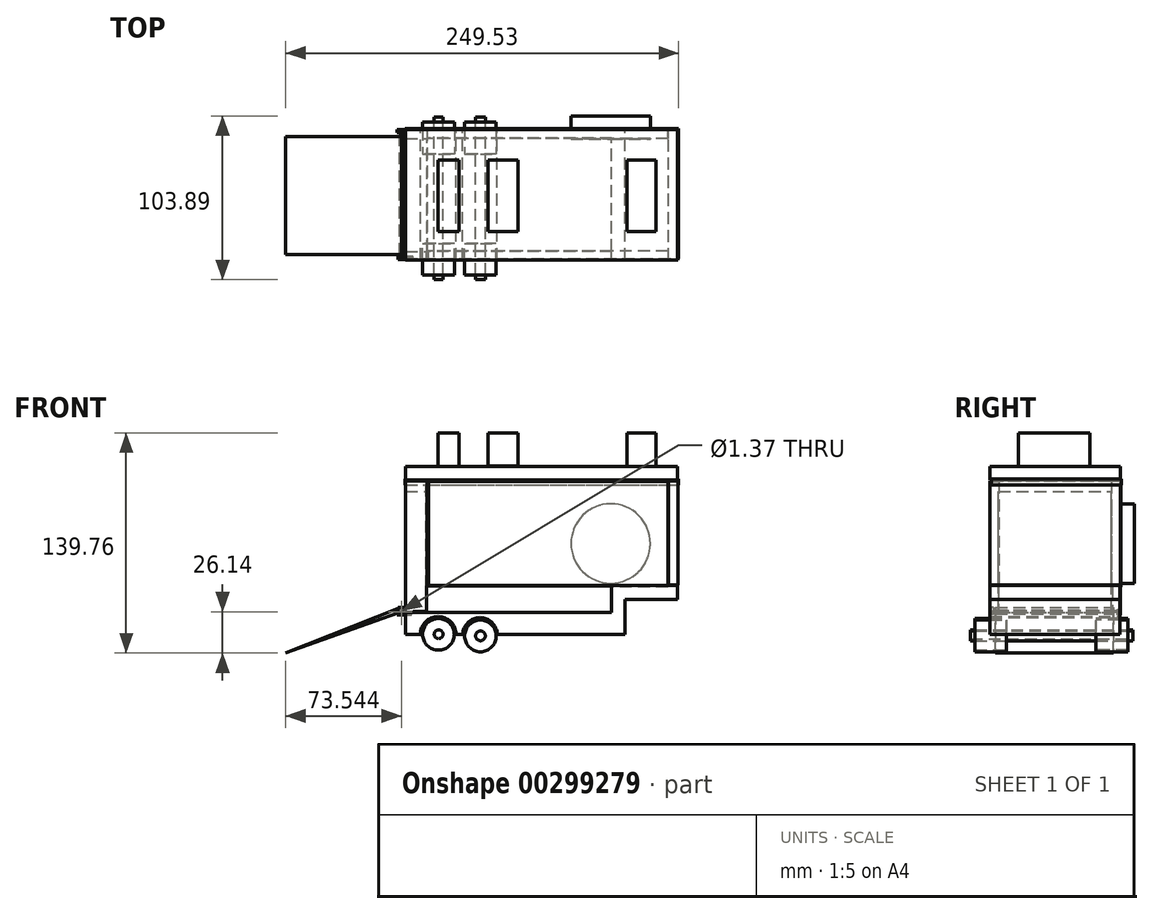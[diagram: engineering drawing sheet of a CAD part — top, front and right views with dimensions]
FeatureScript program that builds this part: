
annotation { "Feature Type Name" : "Feature", "Feature Type Description" : "" }
export const myFeature = defineFeature(function(context is Context, id is Id, definition is map)
    precondition{}
    {
        {
            var Q0;
            Q0=qCreatedBy(makeId("Front.planeOp"),FACE);
            var sketch = newSketch(context, id + "F0", { "sketchPlane" : qUnion([Q0])});
            skLineSegment(sketch, "E0", {"start": v(71.12, -5.98) * mm, "end": v(29.44, -5.98) * mm});
            skLineSegment(sketch, "E1", {"start": v(29.44, -5.98) * mm, "end": v(29.44, -23.17) * mm});
            skLineSegment(sketch, "E2", {"start": v(29.44, -23.17) * mm, "end": v(-101.43, -23.17) * mm});
            skLineSegment(sketch, "E3", {"start": v(-101.43, -23.17) * mm, "end": v(-101.43, -37.16) * mm});
            skLineSegment(sketch, "E4", {"start": v(-101.43, -37.16) * mm, "end": v(37.9, -37.16) * mm});
            skLineSegment(sketch, "E5", {"start": v(37.9, -37.16) * mm, "end": v(37.9, -15.01) * mm});
            skLineSegment(sketch, "E6", {"start": v(37.9, -15.01) * mm, "end": v(71.12, -15.01) * mm});
            skLineSegment(sketch, "E7", {"start": v(71.12, -15.01) * mm, "end": v(71.12, -5.98) * mm});
            skSolve(sketch);
        }
        {
            var Q0;
            Q0 = qSketchRegion(id + "F0", true);
            extrude(context, id + "F1", {"entities" : qUnion([Q0]), "depth" : 38.86 * mm, "hasSecondDirection" : true, "secondDirectionOppositeDirection" : true, "secondDirectionDepth" : 43.43 * mm});
        }
        {
            var Q0;
            Q0=qCreatedBy(makeId("Front.planeOp"),FACE);
            var sketch = newSketch(context, id + "F2", { "sketchPlane" : qUnion([Q0])});
            skCircle(sketch, "E8", {"center": v(-80.74, -37.16) * mm, "radius": 11.34 * mm});
            skCircle(sketch, "E9", {"center": v(-54.21, -37.45) * mm, "radius": 10.96 * mm});
            skSolve(sketch);
        }
        {
            var Q0;
            Q0 = qSketchRegion(id + "F2", true);
            extrude(context, id + "F3", {"entities" : qUnion([Q0]), "operationType" : NewBodyOperationType.REMOVE, "depth" : 43.94 * mm, "hasSecondDirection" : true, "secondDirectionOppositeDirection" : true, "secondDirectionDepth" : 49.28 * mm});
        }
        {
            var Q0;
            Q0=qCreatedBy(makeId("Front.planeOp"),FACE);
            var sketch = newSketch(context, id + "F4", { "sketchPlane" : qUnion([Q0])});
            skLineSegment(sketch, "E10.bottom", {"start": v(29.86, -6.27) * mm, "end": v(-15.61, -6.27) * mm});
            skLineSegment(sketch, "E10.top", {"start": v(29.86, -23.17) * mm, "end": v(-15.61, -23.17) * mm});
            skLineSegment(sketch, "E10.left", {"start": v(29.86, -6.27) * mm, "end": v(29.86, -23.17) * mm});
            skLineSegment(sketch, "E10.right", {"start": v(-15.61, -6.27) * mm, "end": v(-15.61, -23.17) * mm});
            skLineSegment(sketch, "E11.bottom", {"start": v(-15.61, -6.27) * mm, "end": v(-88.2, -6.27) * mm});
            skLineSegment(sketch, "E11.top", {"start": v(-15.61, -23.17) * mm, "end": v(-88.2, -23.17) * mm});
            skLineSegment(sketch, "E11.right", {"start": v(-88.2, -6.27) * mm, "end": v(-88.2, -23.17) * mm});
            skSolve(sketch);
        }
        {
            var Q0;
            Q0 = qSketchRegion(id + "F4", true);
            extrude(context, id + "F5", {"entities" : qUnion([Q0]), "operationType" : NewBodyOperationType.ADD, "depth" : 38.6 * mm, "hasSecondDirection" : true, "secondDirectionOppositeDirection" : false, "secondDirectionDepth" : 33.53 * mm});
        }
        {
            var Q0;
            Q0=qCreatedBy(makeId("Front.planeOp"),FACE);
            var sketch = newSketch(context, id + "F6", { "sketchPlane" : qUnion([Q0])});
            skLineSegment(sketch, "E12.bottom", {"start": v(29.44, -6.56) * mm, "end": v(-22.15, -6.56) * mm});
            skLineSegment(sketch, "E12.top", {"start": v(29.44, -23.17) * mm, "end": v(-22.15, -23.17) * mm});
            skLineSegment(sketch, "E12.left", {"start": v(29.44, -6.56) * mm, "end": v(29.44, -23.17) * mm});
            skLineSegment(sketch, "E12.right", {"start": v(-22.15, -6.56) * mm, "end": v(-22.15, -23.17) * mm});
            skLineSegment(sketch, "E13.bottom", {"start": v(-22.15, -6.56) * mm, "end": v(-88.03, -6.56) * mm});
            skLineSegment(sketch, "E13.top", {"start": v(-22.15, -23.17) * mm, "end": v(-88.03, -23.17) * mm});
            skLineSegment(sketch, "E13.right", {"start": v(-88.03, -6.56) * mm, "end": v(-88.03, -23.17) * mm});
            skSolve(sketch);
        }
        {
            var Q0;
            Q0 = qSketchRegion(id + "F6", true);
            extrude(context, id + "F7", {"entities" : qUnion([Q0]), "operationType" : NewBodyOperationType.ADD, "oppositeDirection" : true, "depth" : 43.43 * mm, "hasSecondDirection" : true, "secondDirectionOppositeDirection" : true, "secondDirectionDepth" : 38.6 * mm});
        }
        {
            var Q0;
            Q0=qCreatedBy(makeId("Right.planeOp"),FACE);
            var sketch = newSketch(context, id + "F8", { "sketchPlane" : qUnion([Q0])});
            skLineSegment(sketch, "E14.bottom", {"start": v(43.93, -23.17) * mm, "end": v(38.1, -23.17) * mm});
            skLineSegment(sketch, "E14.top", {"start": v(43.93, 60.48) * mm, "end": v(38.1, 60.48) * mm});
            skLineSegment(sketch, "E14.left", {"start": v(43.93, -23.17) * mm, "end": v(43.93, 60.48) * mm});
            skLineSegment(sketch, "E14.right", {"start": v(38.1, -23.17) * mm, "end": v(38.1, 60.48) * mm});
            skLineSegment(sketch, "E15.bottom", {"start": v(-33.6, -22.59) * mm, "end": v(-38.56, -22.59) * mm});
            skLineSegment(sketch, "E15.top", {"start": v(-33.6, 60.48) * mm, "end": v(-38.56, 60.48) * mm});
            skLineSegment(sketch, "E15.left", {"start": v(-33.6, -22.59) * mm, "end": v(-33.6, 60.48) * mm});
            skLineSegment(sketch, "E15.right", {"start": v(-38.56, -22.59) * mm, "end": v(-38.56, 60.48) * mm});
            skLineSegment(sketch, "E16.bottom", {"start": v(-33.6, 60.48) * mm, "end": v(38.1, 60.48) * mm});
            skLineSegment(sketch, "E16.top", {"start": v(-33.6, 53.78) * mm, "end": v(38.1, 53.78) * mm});
            skLineSegment(sketch, "E16.left", {"start": v(-33.6, 60.48) * mm, "end": v(-33.6, 53.78) * mm});
            skLineSegment(sketch, "E16.right", {"start": v(38.1, 60.48) * mm, "end": v(38.1, 53.78) * mm});
            skSolve(sketch);
        }
        {
            var Q0;
            Q0 = qSketchRegion(id + "F8", true);
            extrude(context, id + "F9", {"entities" : qUnion([Q0]), "operationType" : NewBodyOperationType.ADD, "oppositeDirection" : true, "depth" : 101.35 * mm, "hasSecondDirection" : true, "secondDirectionOppositeDirection" : true, "secondDirectionDepth" : 87.88 * mm});
        }
        {
            var Q0;
            Q0=qCreatedBy(makeId("Front.planeOp"),FACE);
            var sketch = newSketch(context, id + "F10", { "sketchPlane" : qUnion([Q0])});
            skLineSegment(sketch, "E17", {"start": v(-104.1, -22.8) * mm, "end": v(-177.64, -48.94) * mm});
            skLineSegment(sketch, "E18", {"start": v(-177.64, -48.94) * mm, "end": v(-104.1, -19.93) * mm});
            skLineSegment(sketch, "E19", {"start": v(-104.1, -19.93) * mm, "end": v(-104.1, -22.8) * mm});
            skCircle(sketch, "E20", {"center": v(-104.1, -22.8) * mm, "radius": 0.69 * mm});
            skCircle(sketch, "E21", {"center": v(-104.1, -22.8) * mm, "radius": 1.32 * mm});
            skSolve(sketch);
        }
        {
            var Q0;
            Q0 = qSketchRegion(id + "F10", true);
            extrude(context, id + "F11", {"entities" : qUnion([Q0]), "operationType" : NewBodyOperationType.ADD, "depth" : 35.56 * mm, "hasSecondDirection" : true, "secondDirectionOppositeDirection" : true, "secondDirectionDepth" : 39.37 * mm});
        }
        {
            var Q0;
            Q0=qCreatedBy(makeId("Front.planeOp"),FACE);
            var sketch = newSketch(context, id + "F12", { "sketchPlane" : qUnion([Q0])});
            skLineSegment(sketch, "E22.bottom", {"start": v(71.52, -5.74) * mm, "end": v(65.43, -5.74) * mm});
            skLineSegment(sketch, "E22.top", {"start": v(71.52, 60.34) * mm, "end": v(65.43, 60.34) * mm});
            skLineSegment(sketch, "E22.left", {"start": v(71.52, -5.74) * mm, "end": v(71.52, 60.34) * mm});
            skLineSegment(sketch, "E22.right", {"start": v(65.43, -5.74) * mm, "end": v(65.43, 60.34) * mm});
            skSolve(sketch);
        }
        {
            var Q0;
            Q0 = qSketchRegion(id + "F12", true);
            extrude(context, id + "F13", {"entities" : qUnion([Q0]), "depth" : 39.12 * mm, "hasSecondDirection" : true, "secondDirectionOppositeDirection" : true, "secondDirectionDepth" : 43.94 * mm});
        }
        {
            var Q0;
            Q0=qCreatedBy(makeId("Front.planeOp"),FACE);
            var sketch = newSketch(context, id + "F14", { "sketchPlane" : qUnion([Q0])});
            skLineSegment(sketch, "E23.bottom", {"start": v(65.1, 60.02) * mm, "end": v(0, 60.02) * mm});
            skLineSegment(sketch, "E23.top", {"start": v(65.1, -6.06) * mm, "end": v(0, -6.06) * mm});
            skLineSegment(sketch, "E23.left", {"start": v(65.1, 60.02) * mm, "end": v(65.1, -6.06) * mm});
            skLineSegment(sketch, "E23.right", {"start": v(0, 60.02) * mm, "end": v(0, -6.06) * mm});
            skLineSegment(sketch, "E24.bottom", {"start": v(0, 60.02) * mm, "end": v(-86.94, 60.02) * mm});
            skLineSegment(sketch, "E24.top", {"start": v(0, -6.06) * mm, "end": v(-86.94, -6.06) * mm});
            skLineSegment(sketch, "E24.right", {"start": v(-86.94, 60.02) * mm, "end": v(-86.94, -6.06) * mm});
            skSolve(sketch);
        }
        {
            var Q0;
            Q0 = qSketchRegion(id + "F14", true);
            extrude(context, id + "F15", {"entities" : qUnion([Q0]), "operationType" : NewBodyOperationType.ADD, "depth" : 39.12 * mm, "hasSecondDirection" : true, "secondDirectionOppositeDirection" : false, "secondDirectionDepth" : 33.27 * mm});
        }
        {
            var Q0;
            Q0=qCreatedBy(makeId("Front.planeOp"),FACE);
            var sketch = newSketch(context, id + "F16", { "sketchPlane" : qUnion([Q0])});
            skLineSegment(sketch, "E25.bottom", {"start": v(65.1, 60.02) * mm, "end": v(0, 60.02) * mm});
            skLineSegment(sketch, "E25.top", {"start": v(65.1, -7.02) * mm, "end": v(0, -7.02) * mm});
            skLineSegment(sketch, "E25.left", {"start": v(65.1, 60.02) * mm, "end": v(65.1, -7.02) * mm});
            skLineSegment(sketch, "E25.right", {"start": v(0, 60.02) * mm, "end": v(0, -7.02) * mm});
            skLineSegment(sketch, "E26.bottom", {"start": v(0, 60.02) * mm, "end": v(-88.54, 60.02) * mm});
            skLineSegment(sketch, "E26.top", {"start": v(0, -7.02) * mm, "end": v(-88.54, -7.02) * mm});
            skLineSegment(sketch, "E26.right", {"start": v(-88.54, 60.02) * mm, "end": v(-88.54, -7.02) * mm});
            skSolve(sketch);
        }
        {
            var Q0;
            Q0 = qSketchRegion(id + "F16", true);
            extrude(context, id + "F17", {"entities" : qUnion([Q0]), "operationType" : NewBodyOperationType.ADD, "oppositeDirection" : true, "depth" : 44.2 * mm, "hasSecondDirection" : true, "secondDirectionOppositeDirection" : true, "secondDirectionDepth" : 38.1 * mm});
        }
        {
            var Q0;
            Q0=qCreatedBy(makeId("Front.planeOp"),FACE);
            var sketch = newSketch(context, id + "F18", { "sketchPlane" : qUnion([Q0])});
            skLineSegment(sketch, "E27.bottom", {"start": v(71.11, 60.98) * mm, "end": v(-29.61, 60.98) * mm});
            skLineSegment(sketch, "E27.top", {"start": v(71.11, 69.64) * mm, "end": v(-29.61, 69.64) * mm});
            skLineSegment(sketch, "E27.left", {"start": v(71.11, 60.98) * mm, "end": v(71.11, 69.64) * mm});
            skLineSegment(sketch, "E27.right", {"start": v(-29.61, 60.98) * mm, "end": v(-29.61, 69.64) * mm});
            skLineSegment(sketch, "E28.bottom", {"start": v(-29.61, 60.98) * mm, "end": v(-101.46, 60.98) * mm});
            skLineSegment(sketch, "E28.top", {"start": v(-29.61, 69.64) * mm, "end": v(-101.46, 69.64) * mm});
            skLineSegment(sketch, "E28.right", {"start": v(-101.46, 60.98) * mm, "end": v(-101.46, 69.64) * mm});
            skSolve(sketch);
        }
        {
            var Q0;
            Q0 = qSketchRegion(id + "F18", true);
            extrude(context, id + "F19", {"entities" : qUnion([Q0]), "depth" : 38.86 * mm, "hasSecondDirection" : true, "secondDirectionOppositeDirection" : true, "secondDirectionDepth" : 43.94 * mm});
        }
        {
            var Q0;
            Q0=qCreatedBy(makeId("Front.planeOp"),FACE);
            var sketch = newSketch(context, id + "F20", { "sketchPlane" : qUnion([Q0])});
            skLineSegment(sketch, "E29.bottom", {"start": v(-67.37, 68.68) * mm, "end": v(-80.85, 68.68) * mm});
            skLineSegment(sketch, "E29.top", {"start": v(-67.37, 90.82) * mm, "end": v(-80.85, 90.82) * mm});
            skLineSegment(sketch, "E29.left", {"start": v(-67.37, 68.68) * mm, "end": v(-67.37, 90.82) * mm});
            skLineSegment(sketch, "E29.right", {"start": v(-80.85, 68.68) * mm, "end": v(-80.85, 90.82) * mm});
            skLineSegment(sketch, "E30.bottom", {"start": v(-30.16, 69.97) * mm, "end": v(-49.09, 69.97) * mm});
            skLineSegment(sketch, "E30.top", {"start": v(-30.16, 90.82) * mm, "end": v(-49.09, 90.82) * mm});
            skLineSegment(sketch, "E30.left", {"start": v(-30.16, 69.97) * mm, "end": v(-30.16, 90.82) * mm});
            skLineSegment(sketch, "E30.right", {"start": v(-49.09, 69.97) * mm, "end": v(-49.09, 90.82) * mm});
            skLineSegment(sketch, "E31.bottom", {"start": v(57.73, 69.64) * mm, "end": v(39.12, 69.64) * mm});
            skLineSegment(sketch, "E31.top", {"start": v(57.73, 90.82) * mm, "end": v(39.12, 90.82) * mm});
            skLineSegment(sketch, "E31.left", {"start": v(57.73, 69.64) * mm, "end": v(57.73, 90.82) * mm});
            skLineSegment(sketch, "E31.right", {"start": v(39.12, 69.64) * mm, "end": v(39.12, 90.82) * mm});
            skSolve(sketch);
        }
        {
            var Q0;
            Q0 = qSketchRegion(id + "F20", true);
            extrude(context, id + "F21", {"entities" : qUnion([Q0]), "operationType" : NewBodyOperationType.ADD, "depth" : 20.83 * mm, "hasSecondDirection" : true, "secondDirectionOppositeDirection" : true, "secondDirectionDepth" : 24.38 * mm});
        }
        {
            var Q0;
            Q0=qCreatedBy(makeId("Front.planeOp"),FACE);
            var sketch = newSketch(context, id + "F22", { "sketchPlane" : qUnion([Q0])});
            skLineSegment(sketch, "E32.bottom", {"start": v(-101.88, 61.45) * mm, "end": v(71.9, 61.45) * mm});
            skLineSegment(sketch, "E32.top", {"start": v(-101.88, 57.94) * mm, "end": v(71.9, 57.94) * mm});
            skLineSegment(sketch, "E32.left", {"start": v(-101.88, 61.45) * mm, "end": v(-101.88, 57.94) * mm});
            skLineSegment(sketch, "E32.right", {"start": v(71.9, 61.45) * mm, "end": v(71.9, 57.94) * mm});
            skSolve(sketch);
        }
        {
            var Q0;
            Q0 = qSketchRegion(id + "F22", true);
            extrude(context, id + "F23", {"entities" : qUnion([Q0]), "depth" : 38.1 * mm, "hasSecondDirection" : true, "secondDirectionOppositeDirection" : true, "secondDirectionDepth" : 44.45 * mm});
        }
        {
            var Q0;
            Q0 = qSketchRegion(id + "F10", true);
            extrude(context, id + "F24", {"entities" : qUnion([Q0]), "operationType" : NewBodyOperationType.ADD, "depth" : 25.4 * mm});
        }
        {
            var Q0;
            Q0=makeQuery(id+"F9.opExtrude","SWEPT_FACE",FACE,{"disambiguationData":[OSD([sQuery(id+"F8.wireOp",EDGE,"E14.left")])]});
            var sketch = newSketch(context, id + "F25", { "sketchPlane" : qUnion([Q0])});
            skLineSegment(sketch, "E33.bottom", {"start": v(97.8, -21.28) * mm, "end": v(107.02, -21.28) * mm});
            skLineSegment(sketch, "E33.top", {"start": v(97.8, -24.66) * mm, "end": v(107.02, -24.66) * mm});
            skLineSegment(sketch, "E33.left", {"start": v(97.8, -21.28) * mm, "end": v(97.8, -24.66) * mm});
            skLineSegment(sketch, "E33.right", {"start": v(107.02, -21.28) * mm, "end": v(107.02, -24.66) * mm});
            skSolve(sketch);
        }
        {
            var Q0;
            Q0 = qSketchRegion(id + "F25", true);
            extrude(context, id + "F26", {"entities" : qUnion([Q0]), "operationType" : NewBodyOperationType.ADD, "oppositeDirection" : true, "depth" : 2.03 * mm});
        }
        {
            var Q0;
            Q0=makeQuery(id+"F9.opExtrude","SWEPT_FACE",FACE,{"disambiguationData":[OSD([sQuery(id+"F8.wireOp",EDGE,"E15.right")])]});
            var sketch = newSketch(context, id + "F27", { "sketchPlane" : qUnion([Q0])});
            skLineSegment(sketch, "E34.bottom", {"start": v(-96.63, -20.14) * mm, "end": v(-106.18, -20.14) * mm});
            skLineSegment(sketch, "E34.top", {"start": v(-96.63, -24.5) * mm, "end": v(-106.18, -24.5) * mm});
            skLineSegment(sketch, "E34.left", {"start": v(-96.63, -20.14) * mm, "end": v(-96.63, -24.5) * mm});
            skLineSegment(sketch, "E34.right", {"start": v(-106.18, -20.14) * mm, "end": v(-106.18, -24.5) * mm});
            skSolve(sketch);
        }
        {
            var Q0;
            Q0 = qSketchRegion(id + "F27", true);
            extrude(context, id + "F28", {"entities" : qUnion([Q0]), "operationType" : NewBodyOperationType.ADD, "oppositeDirection" : true, "depth" : 1.78 * mm});
        }
        {
            var Q0;
            Q0=makeQuery(id+"F28.boolean.opBoolean","MERGE",FACE,{"derivedFrom":[makeQuery(id+"F9.opExtrude","SWEPT_FACE",FACE,{"disambiguationData":[OSD([sQuery(id+"F8.wireOp",EDGE,"E15.right")])]}),makeQuery(id+"F28.opExtrude","CAP_FACE",FACE,{"disambiguationData":[OSD([sQuery(id+"F27.wireOp",EDGE,"E34.bottom"),sQuery(id+"F27.wireOp",EDGE,"E34.top"),sQuery(id+"F27.wireOp",EDGE,"E34.left"),sQuery(id+"F27.wireOp",EDGE,"E34.right")])],"isStart":true})]});
            var sketch = newSketch(context, id + "F29", { "sketchPlane" : qUnion([Q0])});
            skCircle(sketch, "E35", {"center": v(-104.09, -22.82) * mm, "radius": 0.5 * mm});
            skSolve(sketch);
        }
        {
            var Q0;
            Q0 = qSketchRegion(id + "F29", true);
            extrude(context, id + "F30", {"entities" : qUnion([Q0]), "operationType" : NewBodyOperationType.ADD, "oppositeDirection" : true, "depth" : 81.28 * mm});
        }
        {
            var Q0;
            Q0=qCreatedBy(makeId("Front.planeOp"),FACE);
            var sketch = newSketch(context, id + "F31", { "sketchPlane" : qUnion([Q0])});
            skCircle(sketch, "E36", {"center": v(-53.93, -38.1) * mm, "radius": 10.05 * mm});
            skCircle(sketch, "E37", {"center": v(-80.57, -37.1) * mm, "radius": 10.05 * mm});
            skSolve(sketch);
        }
        {
            var Q0;
            Q0 = qSketchRegion(id + "F31", true);
            extrude(context, id + "F32", {"entities" : qUnion([Q0]), "depth" : 48.5 * mm, "hasSecondDirection" : true, "secondDirectionOppositeDirection" : false, "secondDirectionDepth" : 28.45 * mm});
        }
        {
            var Q0;
            Q0=makeQuery(id+"F32.opExtrude","SWEPT_BODY",BODY,{"disambiguationData":[OSD([sQuery(id+"F31.wireOp",EDGE,"E36")])]});
            var Q1;
            Q1=makeQuery(id+"F32.opExtrude","SWEPT_BODY",BODY,{"disambiguationData":[OSD([sQuery(id+"F31.wireOp",EDGE,"E37")])]});
            var Q2;
            Q2=qCreatedBy(makeId("Front.planeOp"),FACE);
            mirror(context, id + "F33", {"entities" : qUnion([Q0, Q1]), "mirrorPlane" : qUnion([Q2])});
        }
        {
            var Q0;
            Q0=qCreatedBy(makeId("Front.planeOp"),FACE);
            var sketch = newSketch(context, id + "F34", { "sketchPlane" : qUnion([Q0])});
            skCircle(sketch, "E38", {"center": v(-53.88, -38.05) * mm, "radius": 3.09 * mm});
            skCircle(sketch, "E39", {"center": v(-80.47, -37.04) * mm, "radius": 2.8 * mm});
            skSolve(sketch);
        }
        {
            var Q0;
            Q0 = qSketchRegion(id + "F34", true);
            extrude(context, id + "F35", {"entities" : qUnion([Q0]), "depth" : 51.3 * mm, "hasSecondDirection" : true, "secondDirectionOppositeDirection" : true, "secondDirectionDepth" : 51.92 * mm});
        }
        {
            var Q0;
            Q0=makeQuery(id+"F17.opExtrude","CAP_FACE",FACE,{"disambiguationData":[OSD([sQuery(id+"F16.wireOp",EDGE,"E25.bottom"),sQuery(id+"F16.wireOp",EDGE,"E25.top"),sQuery(id+"F16.wireOp",EDGE,"E25.left"),sQuery(id+"F16.wireOp",EDGE,"E26.bottom"),sQuery(id+"F16.wireOp",EDGE,"E26.top"),sQuery(id+"F16.wireOp",EDGE,"E26.right")])],"isStart":false});
            var sketch = newSketch(context, id + "F36", { "sketchPlane" : qUnion([Q0])});
            skCircle(sketch, "E40", {"center": v(-28.82, 20.56) * mm, "radius": 25.2 * mm});
            skSolve(sketch);
        }
        {
            var Q0;
            Q0 = qSketchRegion(id + "F36", true);
            extrude(context, id + "F37", {"entities" : qUnion([Q0]), "operationType" : NewBodyOperationType.ADD, "depth" : 8.38 * mm, "hasSecondDirection" : true, "secondDirectionOppositeDirection" : true, "secondDirectionDepth" : 6.35 * mm});
        }
    });
